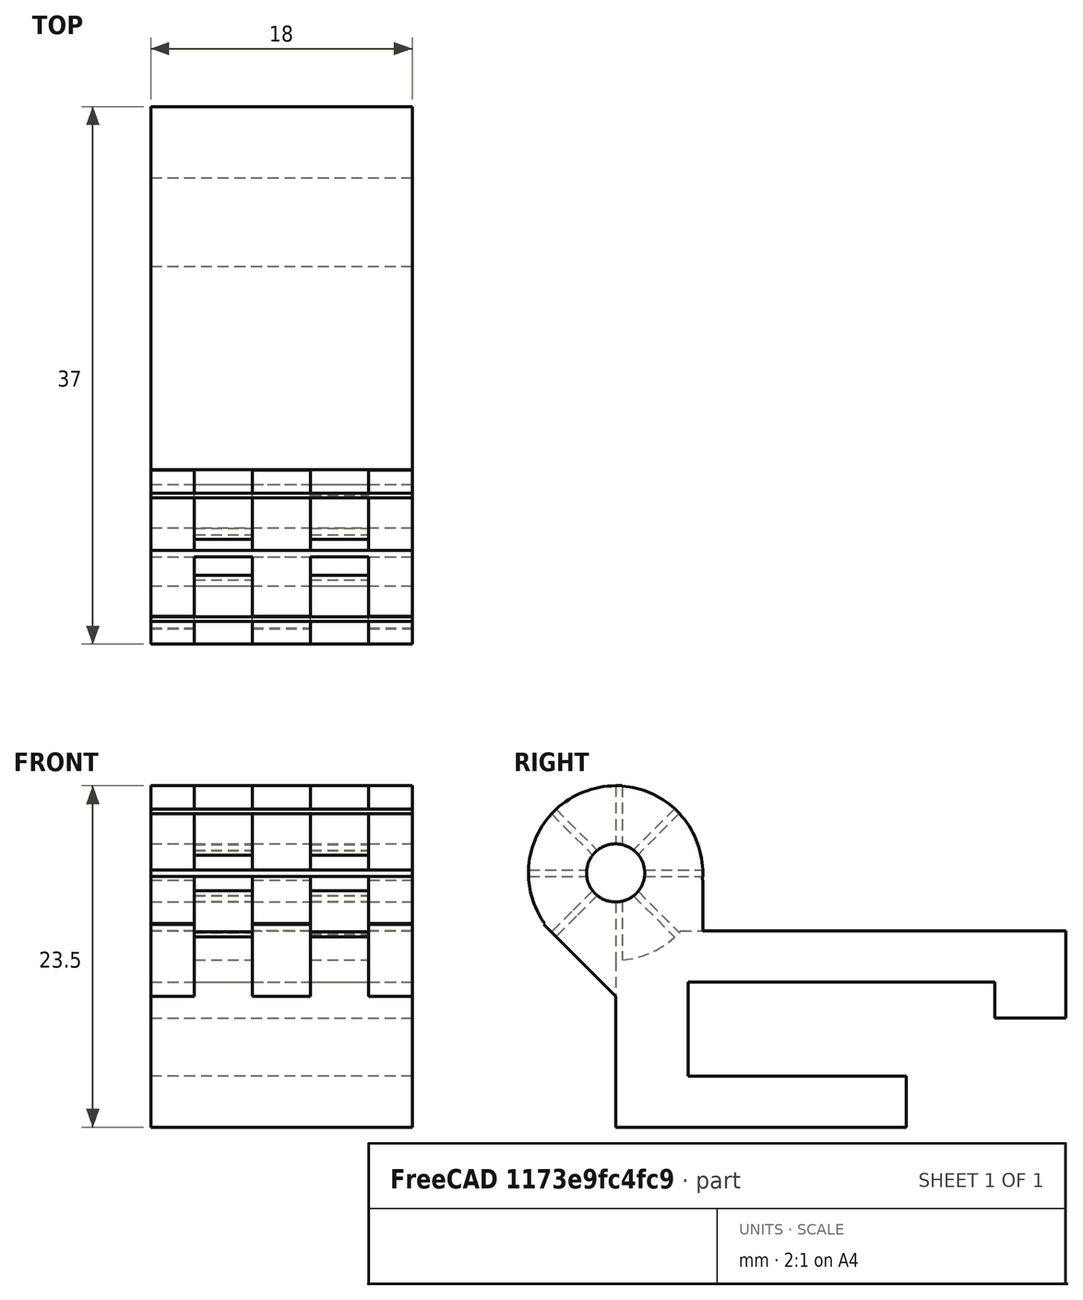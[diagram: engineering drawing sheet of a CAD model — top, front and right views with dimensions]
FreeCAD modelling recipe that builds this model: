
FCSTD DOCUMENT
Label: Fan_accroche
objects: Part::Box×14, Part::Fuse×13, Part::Cut×5, Part::Cylinder×5, Mesh::Feature×1
note: 37 computed .brp shape members not serialized (recipe doc carries the construction recipe); baked Part::Feature solids carry a one-line shape summary decoded from their .brp

FEATURE [Mesh::Feature] fan_mount_mount
  Placement = pos=(0,-45,0) rot=(0,0,1;0rad)
FEATURE [Part::Box] Box
  Height = 13.5
  Length = 18
  Placement = pos=(0,-17,0) rot=(0,0,1;0rad)
  Width = 43
FEATURE [Part::Box] Box001
  Height = 6.5
  Length = 20
  Placement = pos=(-1,0,3.5) rot=(0,0,1;0rad)
  Width = 21.1
FEATURE [Part::Box] Box002
  Height = 7.5
  Length = 20
  Placement = pos=(-1,15,0) rot=(0,0,1;0rad)
  Width = 20
FEATURE [Part::Cut] Cut
  Base = -> Box
  Tool = -> Box001
FEATURE [Part::Cut] Cut001  label="Base1 - crochet"
  Base = -> Cut
  Tool = -> Box002
FEATURE [Part::Cylinder] Cylinder
  Angle = 360
  Height = 4
  Placement = pos=(7,-5,17.5) rot=(0,1,0;1.5708rad)
  Radius = 6
FEATURE [Part::Cylinder] Cylinder002
  Angle = 360
  Height = 3
  Placement = pos=(0,-5,17.5) rot=(0,1,0;1.5708rad)
  Radius = 6
FEATURE [Part::Cylinder] Cylinder001001  label="Trou axe rotation"
  Angle = 360
  Height = 19
  Placement = pos=(0,-5,17.5) rot=(0,1,0;1.5708rad)
  Radius = 2
FEATURE [Part::Cylinder] Cylinder002001
  Angle = 360
  Height = 3
  Placement = pos=(15,-5,17.5) rot=(0,1,0;1.5708rad)
  Radius = 6
FEATURE [Part::Box] Box003
  Height = 14
  Length = 18
  Placement = pos=(0,-18,0) rot=(0,0,1;0rad)
  Width = 13
FEATURE [Part::Cut] Cut002  label="Base2"
  Base = -> Cut001
  Tool = -> Box003
FEATURE [Part::Box] Box004
  Height = 7
  Length = 3
  Placement = pos=(0,-1,10) rot=(0,0,1;0rad)
  Width = 2
FEATURE [Part::Box] Box004001
  Height = 7
  Length = 3
  Placement = pos=(15,-1,10) rot=(0,0,1;0rad)
  Width = 2
FEATURE [Part::Box] Box004002
  Height = 7
  Length = 4
  Placement = pos=(7,-1,10) rot=(0,0,1;0rad)
  Width = 2
FEATURE [Part::Box] Box004001001
  Height = 7
  Length = 3
  Placement = pos=(15,-5,9) rot=(1,0,0;0.785397rad)
  Width = 2
FEATURE [Part::Box] Box004001002
  Height = 7
  Length = 3
  Placement = pos=(0,-5,9) rot=(1,0,0;0.785397rad)
  Width = 2
FEATURE [Part::Box] Box004002001
  Height = 7
  Length = 4
  Placement = pos=(7,-5,9) rot=(1,0,0;0.785397rad)
  Width = 2
FEATURE [Part::Box] Box004002002  label="A decouper1"
  Height = 12
  Length = 18
  Placement = pos=(0,0,-6) rot=(0,0,1;0rad)
  Width = 0.45
FEATURE [Part::Box] Box004002002001  label="A decouper002"
  Height = 12
  Length = 18
  Placement = pos=(0,6,-0.25) rot=(1,0,0;1.5708rad)
  Width = 0.45
FEATURE [Part::Box] Box004002002002  label="A decouper003"
  Height = 12
  Length = 18
  Placement = pos=(0,4.06586,-4.41942) rot=(1,0,0;0.785397rad)
  Width = 0.45
FEATURE [Part::Box] Box004002002003  label="A decouper004"
  Height = 12
  Length = 18
  Placement = pos=(0,-4.41942,-4.06586) rot=(-1,0,0;0.785397rad)
  Width = 0.45
FEATURE [Part::Fuse] Fusion
  Base = -> Box004002002
  Tool = -> Box004002002001
FEATURE [Part::Fuse] Fusion001
  Base = -> Fusion
  Tool = -> Box004002002002
FEATURE [Part::Fuse] Fusion002  label="A decouper"
  Base = -> Fusion001
  Placement = pos=(0,-5,17.5) rot=(0,0,1;0rad)
  Tool = -> Box004002002003
FEATURE [Part::Fuse] Fusion003
  Base = -> Cylinder
  Tool = -> Cylinder002
FEATURE [Part::Fuse] Fusion004
  Base = -> Fusion003
  Tool = -> Cylinder002001
FEATURE [Part::Fuse] Fusion005
  Base = -> Fusion004
  Tool = -> Box004
FEATURE [Part::Fuse] Fusion006
  Base = -> Fusion005
  Tool = -> Box004001
FEATURE [Part::Fuse] Fusion007
  Base = -> Fusion006
  Tool = -> Box004002
FEATURE [Part::Fuse] Fusion008
  Base = -> Fusion007
  Tool = -> Box004001001
FEATURE [Part::Fuse] Fusion009
  Base = -> Fusion008
  Tool = -> Box004001002
FEATURE [Part::Fuse] Fusion010
  Base = -> Fusion009
  Tool = -> Box004002001
FEATURE [Part::Fuse] Fusion011
  Base = -> Fusion002
  Tool = -> Fusion010
FEATURE [Part::Cut] Cut003  label="Excroissance axe rotation"
  Base = -> Fusion011
  Tool = -> Cylinder001001
FEATURE [Part::Cylinder] Cylinder002002  label="Creux axe de rotation"
  Angle = 360
  Height = 20
  Placement = pos=(-1,-5,17.5) rot=(0,1,0;1.5708rad)
  Radius = 6
FEATURE [Part::Cut] Cut004  label="Base3"
  Base = -> Cut002
  Tool = -> Cylinder002002
FEATURE [Part::Fuse] Fusion012  label="Base4"
  Base = -> Cut004
  Tool = -> Cut003
